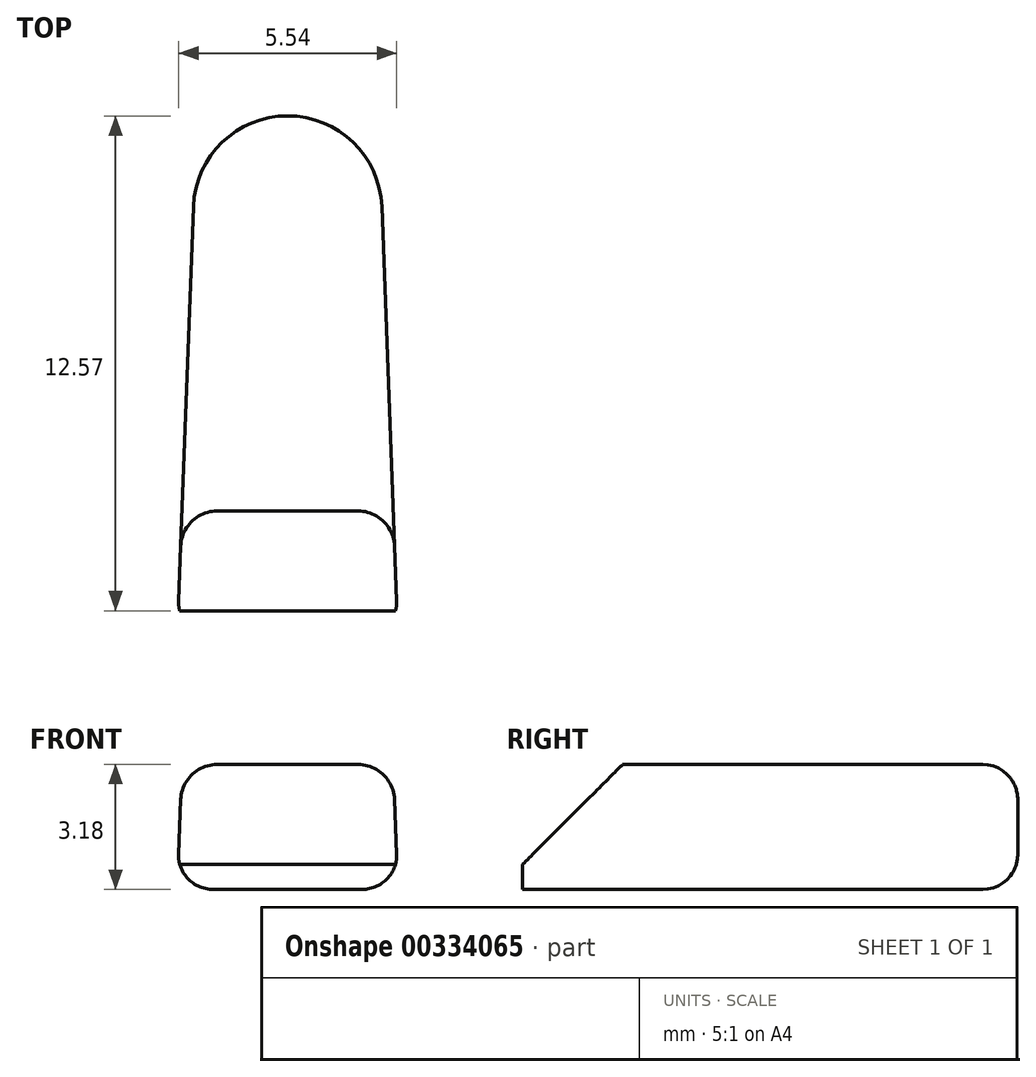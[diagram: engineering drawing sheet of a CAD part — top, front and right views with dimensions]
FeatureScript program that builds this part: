
annotation { "Feature Type Name" : "Feature", "Feature Type Description" : "" }
export const myFeature = defineFeature(function(context is Context, id is Id, definition is map)
    precondition{}
    {
        {
            var Q0;
            Q0=qCreatedBy(makeId("Top.planeOp"),FACE);
            var sketch = newSketch(context, id + "F0", { "sketchPlane" : qUnion([Q0])});
            skPoint(sketch, "E0.visualSharp", {"position": v(22.04, -8.14) * mm});
            skPoint(sketch, "E1.visualSharp", {"position": v(28.84, -9.56) * mm});
            skPoint(sketch, "E2.visualSharp", {"position": v(25.9, -2.41) * mm});
            skLineSegment(sketch, "E3.MirrorCS", {"start": v(-21.92, -8.3) * mm, "end": v(-23.04, -8.54) * mm});
            skLineSegment(sketch, "E4.MirrorCS", {"start": v(-25.67, -9.09) * mm, "end": v(-27.2, -9.4) * mm});
            skArc(sketch, "E5", {"start": v(2.85, 31.56) * mm, "mid": v(0.46, 33.86) * mm, "end": v(-1.94, 31.56) * mm});
            skPoint(sketch, "E6.orphan", {"position": v(0.46, 23.83) * mm});
            skPoint(sketch, "E7.orphan", {"position": v(0.46, 27.64) * mm});
            skPoint(sketch, "E8.visualSharp", {"position": v(4.9, -23.16) * mm});
            skPoint(sketch, "E9.visualSharp", {"position": v(-3.99, -23.16) * mm});
            skPoint(sketch, "E10", {"position": v(0.46, 37.04) * mm});
            skPoint(sketch, "E11.orphan", {"position": v(-2.32, 21.29) * mm});
            skPoint(sketch, "E12.orphan", {"position": v(3.23, 21.29) * mm});
            skPoint(sketch, "E13", {"position": v(3.63, 24.46) * mm});
            skLineSegment(sketch, "E14", {"start": v(-1.94, 31.56) * mm, "end": v(-2.32, 21.29) * mm});
            skLineSegment(sketch, "E15", {"start": v(2.85, 31.56) * mm, "end": v(3.23, 21.29) * mm});
            skLineSegment(sketch, "E16.0", {"start": v(-2.32, 21.29) * mm, "end": v(3.23, 21.29) * mm});
            skSolve(sketch);
        }
        {
            var Q0;
            Q0=makeQuery(id+"F0.imprint","IMPRINT",FACE,{"disambiguationData":[TD([[makeQuery(id+"F0.imprint","IMPRINT",EDGE,{"derivedFrom":sQuery(id+"F0.wireOp",EDGE,"E5")}),1.0]])]});
            extrude(context, id + "F1", {"entities" : qUnion([Q0]), "depth" : 3.17 * mm});
        }
        {
            var Q0;
            Q0=makeQuery(id+"F1.opExtrude","CAP_EDGE",EDGE,{"disambiguationData":[OSD([sQuery(id+"F0.wireOp",EDGE,"E16.0")])],"isStart":false});
            chamfer(context, id + "F2", {"entities" : qUnion([Q0]), "width" : 2.54 * mm, "tangentPropagation" : true});
        }
        {
            var Q0;
            Q0=makeQuery(id+"F1.opExtrude","CAP_EDGE",EDGE,{"disambiguationData":[OSD([sQuery(id+"F0.wireOp",EDGE,"E14")])],"isStart":false});
            var Q1;
            Q1=makeQuery(id+"F1.opExtrude","CAP_EDGE",EDGE,{"disambiguationData":[OSD([sQuery(id+"F0.wireOp",EDGE,"E14")])],"isStart":true});
            fillet(context, id + "F3", {"entities" : qUnion([Q0, Q1]), "radius" : 0.89 * mm, "tangentPropagation" : true, "allowEdgeOverflow" : false});
        }
    });
